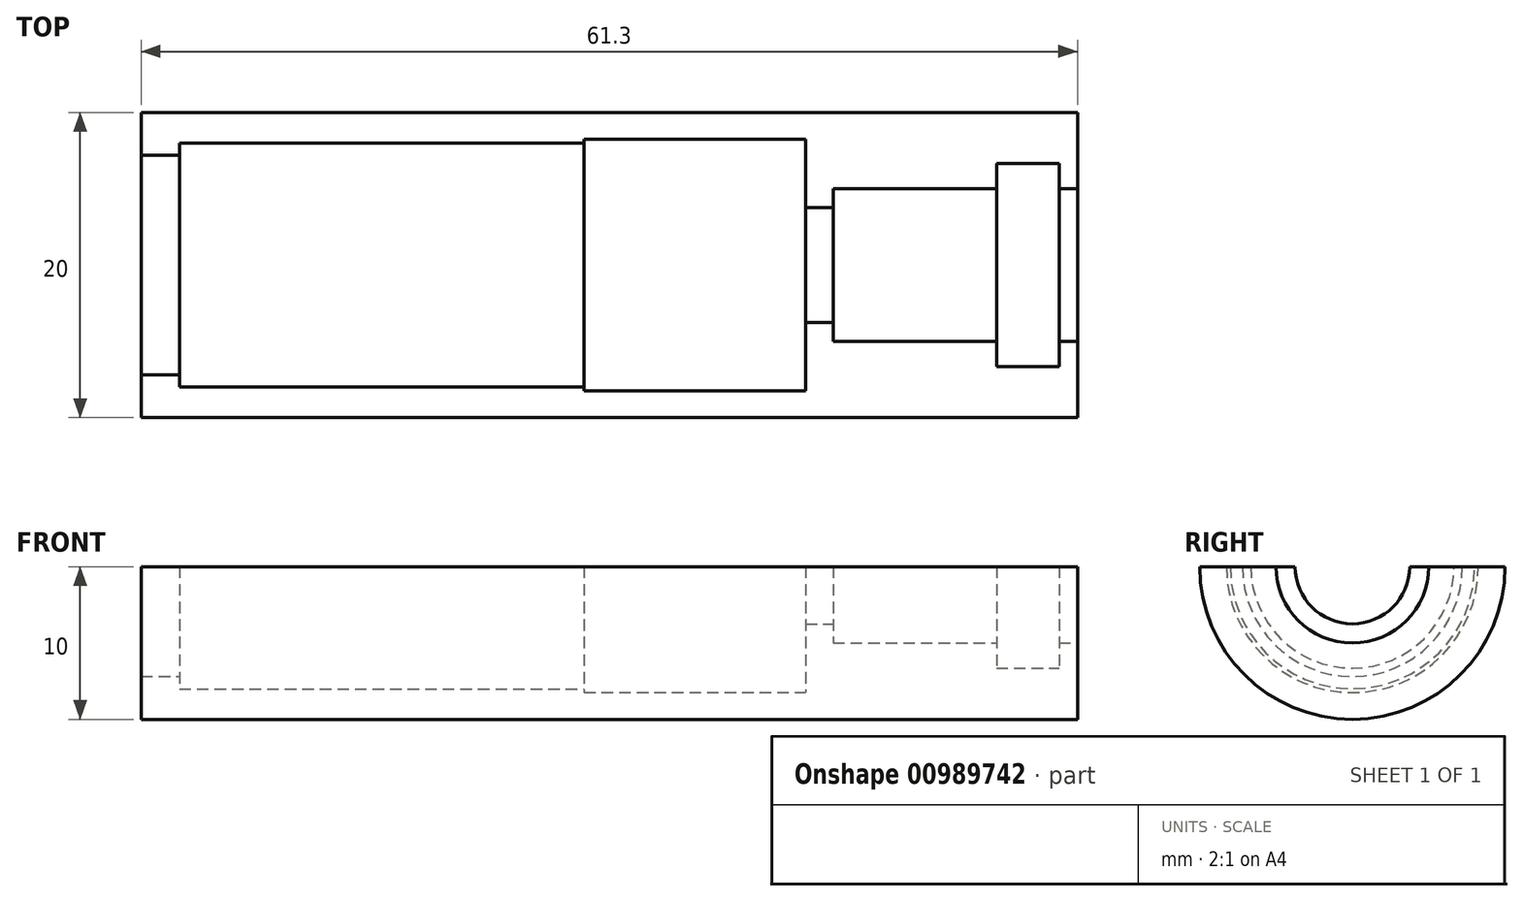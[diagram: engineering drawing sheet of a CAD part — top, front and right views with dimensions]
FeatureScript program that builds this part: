
annotation { "Feature Type Name" : "Feature", "Feature Type Description" : "" }
export const myFeature = defineFeature(function(context is Context, id is Id, definition is map)
    precondition{}
    {
        {
            var Q0;
            Q0=qCreatedBy(makeId("Top.planeOp"),FACE);
            var sketch = newSketch(context, id + "F0", { "sketchPlane" : qUnion([Q0])});
            skLineSegment(sketch, "E0", {"start": v(-9.93, 3.75) * mm, "end": v(-8.13, 3.75) * mm});
            skLineSegment(sketch, "E1", {"start": v(-8.13, 3.75) * mm, "end": v(-8.13, 5) * mm});
            skLineSegment(sketch, "E2", {"start": v(-8.13, 10) * mm, "end": v(-53.43, 10) * mm});
            skLineSegment(sketch, "E3", {"start": v(-53.43, 10) * mm, "end": v(-53.43, 7.2) * mm});
            skLineSegment(sketch, "E4", {"start": v(-53.43, 7.2) * mm, "end": v(-50.93, 7.2) * mm});
            skLineSegment(sketch, "E5", {"start": v(-50.93, 7.2) * mm, "end": v(-50.93, 8) * mm});
            skLineSegment(sketch, "E6", {"start": v(-50.93, 8) * mm, "end": v(-24.43, 8) * mm});
            skLineSegment(sketch, "E7", {"start": v(-24.43, 8) * mm, "end": v(-24.43, 8.25) * mm});
            skLineSegment(sketch, "E8", {"start": v(-24.43, 8.25) * mm, "end": v(-9.93, 8.25) * mm});
            skLineSegment(sketch, "E9", {"start": v(-9.93, 8.25) * mm, "end": v(-9.93, 3.75) * mm});
            skLineSegment(sketch, "E10", {"start": v(46.85, 0) * mm, "end": v(-74.26, 0) * mm, "construction": true});
            skLineSegment(sketch, "E11", {"start": v(-8.13, 5) * mm, "end": v(2.57, 5) * mm});
            skLineSegment(sketch, "E12", {"start": v(2.57, 5) * mm, "end": v(2.57, 6.65) * mm});
            skLineSegment(sketch, "E13", {"start": v(2.57, 6.65) * mm, "end": v(6.67, 6.65) * mm});
            skLineSegment(sketch, "E14", {"start": v(6.67, 6.65) * mm, "end": v(6.67, 5) * mm});
            skLineSegment(sketch, "E15", {"start": v(6.67, 5) * mm, "end": v(7.87, 5) * mm});
            skLineSegment(sketch, "E16", {"start": v(7.87, 5) * mm, "end": v(7.87, 10) * mm});
            skLineSegment(sketch, "E17", {"start": v(7.87, 10) * mm, "end": v(-8.13, 10) * mm});
            skSolve(sketch);
        }
        {
            var Q0;
            Q0=makeQuery(id+"F0.imprint","IMPRINT",FACE,{"disambiguationData":[TD([[makeQuery(id+"F0.imprint","IMPRINT",EDGE,{"derivedFrom":sQuery(id+"F0.wireOp",EDGE,"E0")}),1.0]])]});
            var Q1;
            Q1=sQuery(id+"F0.wireOp",EDGE,"E10");
            revolve(context, id + "F1", {"surfaceOperationType" : NewSurfaceOperationType.NEW, "entities" : qUnion([Q0]), "axis" : qUnion([Q1]), "revolveType" : RevolveType.ONE_DIRECTION, "angle" : 180 * degree});
        }
    });
